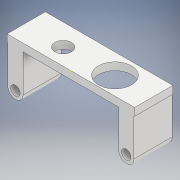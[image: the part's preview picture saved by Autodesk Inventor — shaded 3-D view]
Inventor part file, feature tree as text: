
AUTODESK INVENTOR PART (.ipt)
format: ipt  version: 2018 (Build 220112000, 112)  size: 152,576 bytes
history: native  units: mm
features: extrude x3, sketch x3, projected_geometry x1
ambient origin geometry x8: Origin, YZ Plane, XZ Plane, XY Plane, X Axis, Y Axis, Z Axis, Center Point
bodies: Solid1 (feature_tree)
feature tree (7):
  extrude  "Extrusion1"  Depth=50.0mm
  sketch  "Sketch2"  dims[d2=43.5mm d3=14.635741mm]
  extrude  "Extrusion2"  Depth=43.5mm
  sketch  "Sketch3"  dims[d4=3.7mm d5=3.0mm d6=15.0mm d7=0.0mm d8=6.5mm d9=12.7mm d10=0.0mm d14=34.5mm d15=8.5mm d16=13.0mm d17=8.5mm d18=10.0mm d19=0.0mm d21=15.0mm d22=7.05mm]
  extrude  "Extrusion3"  Depth=3.0mm
  sketch  "Sketch1"  dims[d0=3.0mm d1=50.0mm]
  projected_geometry  "Projected Loop1"
